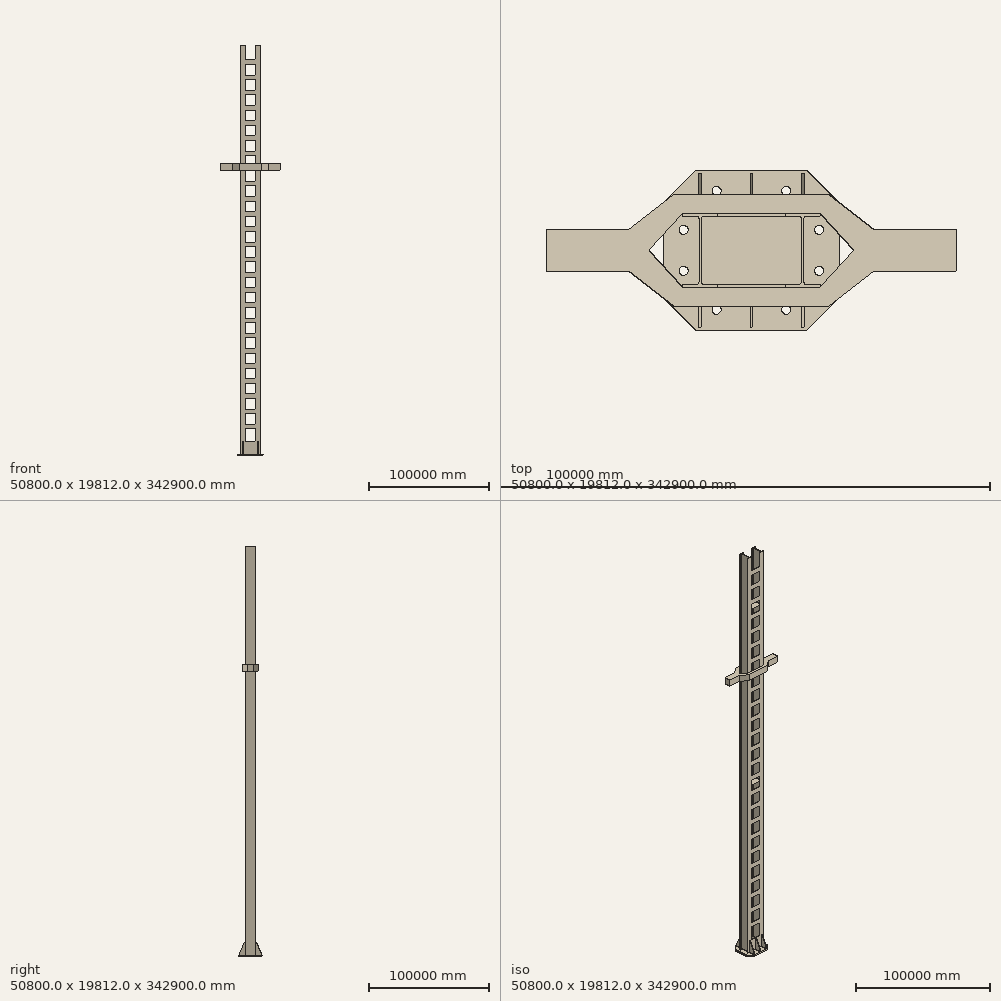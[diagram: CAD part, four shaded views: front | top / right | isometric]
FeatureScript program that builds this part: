
annotation { "Feature Type Name" : "Feature", "Feature Type Description" : "" }
export const myFeature = defineFeature(function(context is Context, id is Id, definition is map)
    precondition{}
    {
        {
            var Q0;
            Q0=qCreatedBy(makeId("Top.planeOp"),FACE);
            var sketch = newSketch(context, id + "F0", { "sketchPlane" : qUnion([Q0])});
            skLineSegment(sketch, "E0", {"start": v(-8509, 4572) * mm, "end": v(8509, 4572) * mm});
            skLineSegment(sketch, "E1", {"start": v(8509, 4572) * mm, "end": v(8509, 4249.42) * mm});
            skLineSegment(sketch, "E2", {"start": v(8509, 4249.42) * mm, "end": v(6908.8, 4249.42) * mm});
            skLineSegment(sketch, "E3", {"start": v(6451.6, 3792.22) * mm, "end": v(6451.6, -3792.22) * mm});
            skLineSegment(sketch, "E4", {"start": v(6908.8, -4249.42) * mm, "end": v(8509, -4249.42) * mm});
            skLineSegment(sketch, "E5", {"start": v(8509, -4249.42) * mm, "end": v(8509, -4572) * mm});
            skLineSegment(sketch, "E6", {"start": v(8509, -4572) * mm, "end": v(-8509, -4572) * mm});
            skLineSegment(sketch, "E7", {"start": v(-8509, -4572) * mm, "end": v(-8509, -4249.42) * mm});
            skLineSegment(sketch, "E8", {"start": v(-8509, -4249.42) * mm, "end": v(-6908.8, -4249.42) * mm});
            skLineSegment(sketch, "E9", {"start": v(-6451.6, -3792.22) * mm, "end": v(-6451.6, 3792.22) * mm});
            skLineSegment(sketch, "E10", {"start": v(-6908.8, 4249.42) * mm, "end": v(-8509, 4249.42) * mm});
            skLineSegment(sketch, "E11", {"start": v(-8509, 4249.42) * mm, "end": v(-8509, 4572) * mm});
            skPoint(sketch, "E12.visualSharp", {"position": v(-6451.6, 4249.42) * mm});
            skArc(sketch, "E12.filletArc", {"start": v(-6451.6, 3792.22) * mm, "mid": v(-6585.51, 4115.5) * mm, "end": v(-6908.8, 4249.42) * mm});
            skPoint(sketch, "E13.visualSharp", {"position": v(6451.6, 4249.42) * mm});
            skArc(sketch, "E13.filletArc", {"start": v(6908.8, 4249.42) * mm, "mid": v(6585.51, 4115.5) * mm, "end": v(6451.6, 3792.22) * mm});
            skPoint(sketch, "E14.visualSharp", {"position": v(6451.6, -4249.42) * mm});
            skArc(sketch, "E14.filletArc", {"start": v(6451.6, -3792.22) * mm, "mid": v(6585.51, -4115.5) * mm, "end": v(6908.8, -4249.42) * mm});
            skPoint(sketch, "E15.visualSharp", {"position": v(-6451.6, -4249.42) * mm});
            skArc(sketch, "E15.filletArc", {"start": v(-6908.8, -4249.42) * mm, "mid": v(-6585.51, -4115.5) * mm, "end": v(-6451.6, -3792.22) * mm});
            skSolve(sketch);
        }
        {
            var Q0;
            Q0=qSketchRegion(id+"F0",true);
            extrude(context, id + "F1", {"entities" : qUnion([Q0]), "depth" : 342900 * mm});
        }
        {
            var Q0;
            Q0=makeQuery(id+"F1.opExtrude","CAP_FACE",FACE,{"disambiguationData":[OSD([sQuery(id+"F0.wireOp",EDGE,"E0"),sQuery(id+"F0.wireOp",EDGE,"E1"),sQuery(id+"F0.wireOp",EDGE,"E2"),sQuery(id+"F0.wireOp",EDGE,"E3"),sQuery(id+"F0.wireOp",EDGE,"E4"),sQuery(id+"F0.wireOp",EDGE,"E5"),sQuery(id+"F0.wireOp",EDGE,"E6"),sQuery(id+"F0.wireOp",EDGE,"E7"),sQuery(id+"F0.wireOp",EDGE,"E8"),sQuery(id+"F0.wireOp",EDGE,"E9"),sQuery(id+"F0.wireOp",EDGE,"E10"),sQuery(id+"F0.wireOp",EDGE,"E11"),sQuery(id+"F0.wireOp",EDGE,"E12.filletArc"),sQuery(id+"F0.wireOp",EDGE,"E13.filletArc"),sQuery(id+"F0.wireOp",EDGE,"E14.filletArc"),sQuery(id+"F0.wireOp",EDGE,"E15.filletArc")])],"isStart":true});
            var sketch = newSketch(context, id + "F2", { "sketchPlane" : qUnion([Q0])});
            skLineSegment(sketch, "E16.bottom", {"start": v(-5791.2, 4249.42) * mm, "end": v(5791.2, 4249.42) * mm});
            skLineSegment(sketch, "E16.top", {"start": v(-5791.2, -4249.42) * mm, "end": v(5791.2, -4249.42) * mm});
            skLineSegment(sketch, "E16.left", {"start": v(-6248.4, 3792.22) * mm, "end": v(-6248.4, -3792.22) * mm});
            skLineSegment(sketch, "E16.right", {"start": v(6248.4, 3792.22) * mm, "end": v(6248.4, -3792.22) * mm});
            skPoint(sketch, "E17.visualSharp", {"position": v(-6248.4, 4249.42) * mm});
            skArc(sketch, "E17.filletArc", {"start": v(-5791.2, 4249.42) * mm, "mid": v(-6114.49, 4115.5) * mm, "end": v(-6248.4, 3792.22) * mm});
            skPoint(sketch, "E18.visualSharp", {"position": v(6248.4, 4249.42) * mm});
            skArc(sketch, "E18.filletArc", {"start": v(6248.4, 3792.22) * mm, "mid": v(6114.49, 4115.5) * mm, "end": v(5791.2, 4249.42) * mm});
            skPoint(sketch, "E19.visualSharp", {"position": v(6248.4, -4249.42) * mm});
            skArc(sketch, "E19.filletArc", {"start": v(5791.2, -4249.42) * mm, "mid": v(6114.49, -4115.5) * mm, "end": v(6248.4, -3792.22) * mm});
            skPoint(sketch, "E20.visualSharp", {"position": v(-6248.4, -4249.42) * mm});
            skArc(sketch, "E20.filletArc", {"start": v(-6248.4, -3792.22) * mm, "mid": v(-6114.49, -4115.5) * mm, "end": v(-5791.2, -4249.42) * mm});
            skLineSegment(sketch, "E21", {"start": v(-6913.3, 0) * mm, "end": v(6813.76, 0) * mm, "construction": true});
            skLineSegment(sketch, "E22", {"start": v(0, 5029.13) * mm, "end": v(0, -5231.93) * mm, "construction": true});
            skSolve(sketch);
        }
        {
            var Q0;
            Q0=qSketchRegion(id+"F2",true);
            extrude(context, id + "F3", {"entities" : qUnion([Q0]), "operationType" : NewBodyOperationType.REMOVE, "endBound" : BoundingType.THROUGH_ALL, "oppositeDirection" : true, "depth" : 25.4 * mm});
        }
        {
            var Q0;
            Q0=makeQuery(id+"F1.opExtrude","SWEPT_FACE",FACE,{"disambiguationData":[OSD([sQuery(id+"F0.wireOp",EDGE,"E6")])]});
            var sketch = newSketch(context, id + "F4", { "sketchPlane" : qUnion([Q0])});
            skLineSegment(sketch, "E23.bottom", {"start": v(-4191, 34925) * mm, "end": v(4191, 34925) * mm});
            skLineSegment(sketch, "E23.top", {"start": v(-4191, 26035) * mm, "end": v(4191, 26035) * mm});
            skLineSegment(sketch, "E23.left", {"start": v(-4191, 34925) * mm, "end": v(-4191, 26035) * mm});
            skLineSegment(sketch, "E23.right", {"start": v(4191, 34925) * mm, "end": v(4191, 26035) * mm});
            skLineSegment(sketch, "E24", {"start": v(0, -2627.58) * mm, "end": v(0, 406140.36) * mm, "construction": true});
            skLineSegment(sketch, "E25.0.1.0", {"start": v(-4191, 47625) * mm, "end": v(4191, 47625) * mm});
            skLineSegment(sketch, "E25.0.1.1", {"start": v(-4191, 38735) * mm, "end": v(4191, 38735) * mm});
            skLineSegment(sketch, "E25.0.1.2", {"start": v(-4191, 47625) * mm, "end": v(-4191, 38735) * mm});
            skLineSegment(sketch, "E25.0.1.3", {"start": v(4191, 47625) * mm, "end": v(4191, 38735) * mm});
            skLineSegment(sketch, "E25.0.2.0", {"start": v(-4191, 60325) * mm, "end": v(4191, 60325) * mm});
            skLineSegment(sketch, "E25.0.2.1", {"start": v(-4191, 51435) * mm, "end": v(4191, 51435) * mm});
            skLineSegment(sketch, "E25.0.2.2", {"start": v(-4191, 60325) * mm, "end": v(-4191, 51435) * mm});
            skLineSegment(sketch, "E25.0.2.3", {"start": v(4191, 60325) * mm, "end": v(4191, 51435) * mm});
            skLineSegment(sketch, "E25.0.3.0", {"start": v(-4191, 73025) * mm, "end": v(4191, 73025) * mm});
            skLineSegment(sketch, "E25.0.3.1", {"start": v(-4191, 64135) * mm, "end": v(4191, 64135) * mm});
            skLineSegment(sketch, "E25.0.3.2", {"start": v(-4191, 73025) * mm, "end": v(-4191, 64135) * mm});
            skLineSegment(sketch, "E25.0.3.3", {"start": v(4191, 73025) * mm, "end": v(4191, 64135) * mm});
            skLineSegment(sketch, "E25.0.4.0", {"start": v(-4191, 85725) * mm, "end": v(4191, 85725) * mm});
            skLineSegment(sketch, "E25.0.4.1", {"start": v(-4191, 76835) * mm, "end": v(4191, 76835) * mm});
            skLineSegment(sketch, "E25.0.4.2", {"start": v(-4191, 85725) * mm, "end": v(-4191, 76835) * mm});
            skLineSegment(sketch, "E25.0.4.3", {"start": v(4191, 85725) * mm, "end": v(4191, 76835) * mm});
            skLineSegment(sketch, "E25.0.5.0", {"start": v(-4191, 98425) * mm, "end": v(4191, 98425) * mm});
            skLineSegment(sketch, "E25.0.5.1", {"start": v(-4191, 89535) * mm, "end": v(4191, 89535) * mm});
            skLineSegment(sketch, "E25.0.5.2", {"start": v(-4191, 98425) * mm, "end": v(-4191, 89535) * mm});
            skLineSegment(sketch, "E25.0.5.3", {"start": v(4191, 98425) * mm, "end": v(4191, 89535) * mm});
            skLineSegment(sketch, "E25.0.6.0", {"start": v(-4191, 111125) * mm, "end": v(4191, 111125) * mm});
            skLineSegment(sketch, "E25.0.6.1", {"start": v(-4191, 102235) * mm, "end": v(4191, 102235) * mm});
            skLineSegment(sketch, "E25.0.6.2", {"start": v(-4191, 111125) * mm, "end": v(-4191, 102235) * mm});
            skLineSegment(sketch, "E25.0.6.3", {"start": v(4191, 111125) * mm, "end": v(4191, 102235) * mm});
            skLineSegment(sketch, "E25.0.7.0", {"start": v(-4191, 123825) * mm, "end": v(4191, 123825) * mm});
            skLineSegment(sketch, "E25.0.7.1", {"start": v(-4191, 114935) * mm, "end": v(4191, 114935) * mm});
            skLineSegment(sketch, "E25.0.7.2", {"start": v(-4191, 123825) * mm, "end": v(-4191, 114935) * mm});
            skLineSegment(sketch, "E25.0.7.3", {"start": v(4191, 123825) * mm, "end": v(4191, 114935) * mm});
            skLineSegment(sketch, "E25.0.8.0", {"start": v(-4191, 136525) * mm, "end": v(4191, 136525) * mm});
            skLineSegment(sketch, "E25.0.8.1", {"start": v(-4191, 127635) * mm, "end": v(4191, 127635) * mm});
            skLineSegment(sketch, "E25.0.8.2", {"start": v(-4191, 136525) * mm, "end": v(-4191, 127635) * mm});
            skLineSegment(sketch, "E25.0.8.3", {"start": v(4191, 136525) * mm, "end": v(4191, 127635) * mm});
            skLineSegment(sketch, "E25.0.9.0", {"start": v(-4191, 149225) * mm, "end": v(4191, 149225) * mm});
            skLineSegment(sketch, "E25.0.9.1", {"start": v(-4191, 140335) * mm, "end": v(4191, 140335) * mm});
            skLineSegment(sketch, "E25.0.9.2", {"start": v(-4191, 149225) * mm, "end": v(-4191, 140335) * mm});
            skLineSegment(sketch, "E25.0.9.3", {"start": v(4191, 149225) * mm, "end": v(4191, 140335) * mm});
            skLineSegment(sketch, "E25.0.10.0", {"start": v(-4191, 161925) * mm, "end": v(4191, 161925) * mm});
            skLineSegment(sketch, "E25.0.10.1", {"start": v(-4191, 153035) * mm, "end": v(4191, 153035) * mm});
            skLineSegment(sketch, "E25.0.10.2", {"start": v(-4191, 161925) * mm, "end": v(-4191, 153035) * mm});
            skLineSegment(sketch, "E25.0.10.3", {"start": v(4191, 161925) * mm, "end": v(4191, 153035) * mm});
            skLineSegment(sketch, "E25.0.11.0", {"start": v(-4191, 174625) * mm, "end": v(4191, 174625) * mm});
            skLineSegment(sketch, "E25.0.11.1", {"start": v(-4191, 165735) * mm, "end": v(4191, 165735) * mm});
            skLineSegment(sketch, "E25.0.11.2", {"start": v(-4191, 174625) * mm, "end": v(-4191, 165735) * mm});
            skLineSegment(sketch, "E25.0.11.3", {"start": v(4191, 174625) * mm, "end": v(4191, 165735) * mm});
            skLineSegment(sketch, "E25.0.12.0", {"start": v(-4191, 187325) * mm, "end": v(4191, 187325) * mm});
            skLineSegment(sketch, "E25.0.12.1", {"start": v(-4191, 178435) * mm, "end": v(4191, 178435) * mm});
            skLineSegment(sketch, "E25.0.12.2", {"start": v(-4191, 187325) * mm, "end": v(-4191, 178435) * mm});
            skLineSegment(sketch, "E25.0.12.3", {"start": v(4191, 187325) * mm, "end": v(4191, 178435) * mm});
            skLineSegment(sketch, "E25.0.13.0", {"start": v(-4191, 200025) * mm, "end": v(4191, 200025) * mm});
            skLineSegment(sketch, "E25.0.13.1", {"start": v(-4191, 191135) * mm, "end": v(4191, 191135) * mm});
            skLineSegment(sketch, "E25.0.13.2", {"start": v(-4191, 200025) * mm, "end": v(-4191, 191135) * mm});
            skLineSegment(sketch, "E25.0.13.3", {"start": v(4191, 200025) * mm, "end": v(4191, 191135) * mm});
            skLineSegment(sketch, "E25.0.14.0", {"start": v(-4191, 212725) * mm, "end": v(4191, 212725) * mm});
            skLineSegment(sketch, "E25.0.14.1", {"start": v(-4191, 203835) * mm, "end": v(4191, 203835) * mm});
            skLineSegment(sketch, "E25.0.14.2", {"start": v(-4191, 212725) * mm, "end": v(-4191, 203835) * mm});
            skLineSegment(sketch, "E25.0.14.3", {"start": v(4191, 212725) * mm, "end": v(4191, 203835) * mm});
            skLineSegment(sketch, "E25.0.15.0", {"start": v(-4191, 225425) * mm, "end": v(4191, 225425) * mm});
            skLineSegment(sketch, "E25.0.15.1", {"start": v(-4191, 216535) * mm, "end": v(4191, 216535) * mm});
            skLineSegment(sketch, "E25.0.15.2", {"start": v(-4191, 225425) * mm, "end": v(-4191, 216535) * mm});
            skLineSegment(sketch, "E25.0.15.3", {"start": v(4191, 225425) * mm, "end": v(4191, 216535) * mm});
            skLineSegment(sketch, "E25.0.16.0", {"start": v(-4191, 238125) * mm, "end": v(4191, 238125) * mm});
            skLineSegment(sketch, "E25.0.16.1", {"start": v(-4191, 229235) * mm, "end": v(4191, 229235) * mm});
            skLineSegment(sketch, "E25.0.16.2", {"start": v(-4191, 238125) * mm, "end": v(-4191, 229235) * mm});
            skLineSegment(sketch, "E25.0.16.3", {"start": v(4191, 238125) * mm, "end": v(4191, 229235) * mm});
            skLineSegment(sketch, "E25.0.17.0", {"start": v(-4191, 250825) * mm, "end": v(4191, 250825) * mm});
            skLineSegment(sketch, "E25.0.17.1", {"start": v(-4191, 241935) * mm, "end": v(4191, 241935) * mm});
            skLineSegment(sketch, "E25.0.17.2", {"start": v(-4191, 250825) * mm, "end": v(-4191, 241935) * mm});
            skLineSegment(sketch, "E25.0.17.3", {"start": v(4191, 250825) * mm, "end": v(4191, 241935) * mm});
            skLineSegment(sketch, "E25.0.18.0", {"start": v(-4191, 263525) * mm, "end": v(4191, 263525) * mm});
            skLineSegment(sketch, "E25.0.18.1", {"start": v(-4191, 254635) * mm, "end": v(4191, 254635) * mm});
            skLineSegment(sketch, "E25.0.18.2", {"start": v(-4191, 263525) * mm, "end": v(-4191, 254635) * mm});
            skLineSegment(sketch, "E25.0.18.3", {"start": v(4191, 263525) * mm, "end": v(4191, 254635) * mm});
            skLineSegment(sketch, "E25.0.19.0", {"start": v(-4191, 276225) * mm, "end": v(4191, 276225) * mm});
            skLineSegment(sketch, "E25.0.19.1", {"start": v(-4191, 267335) * mm, "end": v(4191, 267335) * mm});
            skLineSegment(sketch, "E25.0.19.2", {"start": v(-4191, 276225) * mm, "end": v(-4191, 267335) * mm});
            skLineSegment(sketch, "E25.0.19.3", {"start": v(4191, 276225) * mm, "end": v(4191, 267335) * mm});
            skLineSegment(sketch, "E25.0.20.0", {"start": v(-4191, 288925) * mm, "end": v(4191, 288925) * mm});
            skLineSegment(sketch, "E25.0.20.1", {"start": v(-4191, 280035) * mm, "end": v(4191, 280035) * mm});
            skLineSegment(sketch, "E25.0.20.2", {"start": v(-4191, 288925) * mm, "end": v(-4191, 280035) * mm});
            skLineSegment(sketch, "E25.0.20.3", {"start": v(4191, 288925) * mm, "end": v(4191, 280035) * mm});
            skLineSegment(sketch, "E25.0.21.0", {"start": v(-4191, 301625) * mm, "end": v(4191, 301625) * mm});
            skLineSegment(sketch, "E25.0.21.1", {"start": v(-4191, 292735) * mm, "end": v(4191, 292735) * mm});
            skLineSegment(sketch, "E25.0.21.2", {"start": v(-4191, 301625) * mm, "end": v(-4191, 292735) * mm});
            skLineSegment(sketch, "E25.0.21.3", {"start": v(4191, 301625) * mm, "end": v(4191, 292735) * mm});
            skLineSegment(sketch, "E25.0.22.0", {"start": v(-4191, 314325) * mm, "end": v(4191, 314325) * mm});
            skLineSegment(sketch, "E25.0.22.1", {"start": v(-4191, 305435) * mm, "end": v(4191, 305435) * mm});
            skLineSegment(sketch, "E25.0.22.2", {"start": v(-4191, 314325) * mm, "end": v(-4191, 305435) * mm});
            skLineSegment(sketch, "E25.0.22.3", {"start": v(4191, 314325) * mm, "end": v(4191, 305435) * mm});
            skLineSegment(sketch, "E25.0.23.0", {"start": v(-4191, 327025) * mm, "end": v(4191, 327025) * mm});
            skLineSegment(sketch, "E25.0.23.1", {"start": v(-4191, 318135) * mm, "end": v(4191, 318135) * mm});
            skLineSegment(sketch, "E25.0.23.2", {"start": v(-4191, 327025) * mm, "end": v(-4191, 318135) * mm});
            skLineSegment(sketch, "E25.0.23.3", {"start": v(4191, 327025) * mm, "end": v(4191, 318135) * mm});
            skLineSegment(sketch, "E25.1.1.0", {"start": v(-4191, 47625) * mm, "end": v(4191, 47625) * mm});
            skLineSegment(sketch, "E25.1.1.1", {"start": v(-4191, 38735) * mm, "end": v(4191, 38735) * mm});
            skLineSegment(sketch, "E25.1.1.2", {"start": v(-4191, 47625) * mm, "end": v(-4191, 38735) * mm});
            skLineSegment(sketch, "E25.1.1.3", {"start": v(4191, 47625) * mm, "end": v(4191, 38735) * mm});
            skLineSegment(sketch, "E25.1.2.0", {"start": v(-4191, 60325) * mm, "end": v(4191, 60325) * mm});
            skLineSegment(sketch, "E25.1.2.1", {"start": v(-4191, 51435) * mm, "end": v(4191, 51435) * mm});
            skLineSegment(sketch, "E25.1.2.2", {"start": v(-4191, 60325) * mm, "end": v(-4191, 51435) * mm});
            skLineSegment(sketch, "E25.1.2.3", {"start": v(4191, 60325) * mm, "end": v(4191, 51435) * mm});
            skLineSegment(sketch, "E25.1.3.0", {"start": v(-4191, 73025) * mm, "end": v(4191, 73025) * mm});
            skLineSegment(sketch, "E25.1.3.1", {"start": v(-4191, 64135) * mm, "end": v(4191, 64135) * mm});
            skLineSegment(sketch, "E25.1.3.2", {"start": v(-4191, 73025) * mm, "end": v(-4191, 64135) * mm});
            skLineSegment(sketch, "E25.1.3.3", {"start": v(4191, 73025) * mm, "end": v(4191, 64135) * mm});
            skLineSegment(sketch, "E25.1.4.0", {"start": v(-4191, 85725) * mm, "end": v(4191, 85725) * mm});
            skLineSegment(sketch, "E25.1.4.1", {"start": v(-4191, 76835) * mm, "end": v(4191, 76835) * mm});
            skLineSegment(sketch, "E25.1.4.2", {"start": v(-4191, 85725) * mm, "end": v(-4191, 76835) * mm});
            skLineSegment(sketch, "E25.1.4.3", {"start": v(4191, 85725) * mm, "end": v(4191, 76835) * mm});
            skLineSegment(sketch, "E25.1.5.0", {"start": v(-4191, 98425) * mm, "end": v(4191, 98425) * mm});
            skLineSegment(sketch, "E25.1.5.1", {"start": v(-4191, 89535) * mm, "end": v(4191, 89535) * mm});
            skLineSegment(sketch, "E25.1.5.2", {"start": v(-4191, 98425) * mm, "end": v(-4191, 89535) * mm});
            skLineSegment(sketch, "E25.1.5.3", {"start": v(4191, 98425) * mm, "end": v(4191, 89535) * mm});
            skLineSegment(sketch, "E25.1.6.0", {"start": v(-4191, 111125) * mm, "end": v(4191, 111125) * mm});
            skLineSegment(sketch, "E25.1.6.1", {"start": v(-4191, 102235) * mm, "end": v(4191, 102235) * mm});
            skLineSegment(sketch, "E25.1.6.2", {"start": v(-4191, 111125) * mm, "end": v(-4191, 102235) * mm});
            skLineSegment(sketch, "E25.1.6.3", {"start": v(4191, 111125) * mm, "end": v(4191, 102235) * mm});
            skLineSegment(sketch, "E25.1.7.0", {"start": v(-4191, 123825) * mm, "end": v(4191, 123825) * mm});
            skLineSegment(sketch, "E25.1.7.1", {"start": v(-4191, 114935) * mm, "end": v(4191, 114935) * mm});
            skLineSegment(sketch, "E25.1.7.2", {"start": v(-4191, 123825) * mm, "end": v(-4191, 114935) * mm});
            skLineSegment(sketch, "E25.1.7.3", {"start": v(4191, 123825) * mm, "end": v(4191, 114935) * mm});
            skLineSegment(sketch, "E25.1.8.0", {"start": v(-4191, 136525) * mm, "end": v(4191, 136525) * mm});
            skLineSegment(sketch, "E25.1.8.1", {"start": v(-4191, 127635) * mm, "end": v(4191, 127635) * mm});
            skLineSegment(sketch, "E25.1.8.2", {"start": v(-4191, 136525) * mm, "end": v(-4191, 127635) * mm});
            skLineSegment(sketch, "E25.1.8.3", {"start": v(4191, 136525) * mm, "end": v(4191, 127635) * mm});
            skLineSegment(sketch, "E25.1.9.0", {"start": v(-4191, 149225) * mm, "end": v(4191, 149225) * mm});
            skLineSegment(sketch, "E25.1.9.1", {"start": v(-4191, 140335) * mm, "end": v(4191, 140335) * mm});
            skLineSegment(sketch, "E25.1.9.2", {"start": v(-4191, 149225) * mm, "end": v(-4191, 140335) * mm});
            skLineSegment(sketch, "E25.1.9.3", {"start": v(4191, 149225) * mm, "end": v(4191, 140335) * mm});
            skLineSegment(sketch, "E25.1.10.0", {"start": v(-4191, 161925) * mm, "end": v(4191, 161925) * mm});
            skLineSegment(sketch, "E25.1.10.1", {"start": v(-4191, 153035) * mm, "end": v(4191, 153035) * mm});
            skLineSegment(sketch, "E25.1.10.2", {"start": v(-4191, 161925) * mm, "end": v(-4191, 153035) * mm});
            skLineSegment(sketch, "E25.1.10.3", {"start": v(4191, 161925) * mm, "end": v(4191, 153035) * mm});
            skLineSegment(sketch, "E25.1.11.0", {"start": v(-4191, 174625) * mm, "end": v(4191, 174625) * mm});
            skLineSegment(sketch, "E25.1.11.1", {"start": v(-4191, 165735) * mm, "end": v(4191, 165735) * mm});
            skLineSegment(sketch, "E25.1.11.2", {"start": v(-4191, 174625) * mm, "end": v(-4191, 165735) * mm});
            skLineSegment(sketch, "E25.1.11.3", {"start": v(4191, 174625) * mm, "end": v(4191, 165735) * mm});
            skLineSegment(sketch, "E25.1.12.0", {"start": v(-4191, 187325) * mm, "end": v(4191, 187325) * mm});
            skLineSegment(sketch, "E25.1.12.1", {"start": v(-4191, 178435) * mm, "end": v(4191, 178435) * mm});
            skLineSegment(sketch, "E25.1.12.2", {"start": v(-4191, 187325) * mm, "end": v(-4191, 178435) * mm});
            skLineSegment(sketch, "E25.1.12.3", {"start": v(4191, 187325) * mm, "end": v(4191, 178435) * mm});
            skLineSegment(sketch, "E25.1.13.0", {"start": v(-4191, 200025) * mm, "end": v(4191, 200025) * mm});
            skLineSegment(sketch, "E25.1.13.1", {"start": v(-4191, 191135) * mm, "end": v(4191, 191135) * mm});
            skLineSegment(sketch, "E25.1.13.2", {"start": v(-4191, 200025) * mm, "end": v(-4191, 191135) * mm});
            skLineSegment(sketch, "E25.1.13.3", {"start": v(4191, 200025) * mm, "end": v(4191, 191135) * mm});
            skLineSegment(sketch, "E25.1.14.0", {"start": v(-4191, 212725) * mm, "end": v(4191, 212725) * mm});
            skLineSegment(sketch, "E25.1.14.1", {"start": v(-4191, 203835) * mm, "end": v(4191, 203835) * mm});
            skLineSegment(sketch, "E25.1.14.2", {"start": v(-4191, 212725) * mm, "end": v(-4191, 203835) * mm});
            skLineSegment(sketch, "E25.1.14.3", {"start": v(4191, 212725) * mm, "end": v(4191, 203835) * mm});
            skLineSegment(sketch, "E25.1.15.0", {"start": v(-4191, 225425) * mm, "end": v(4191, 225425) * mm});
            skLineSegment(sketch, "E25.1.15.1", {"start": v(-4191, 216535) * mm, "end": v(4191, 216535) * mm});
            skLineSegment(sketch, "E25.1.15.2", {"start": v(-4191, 225425) * mm, "end": v(-4191, 216535) * mm});
            skLineSegment(sketch, "E25.1.15.3", {"start": v(4191, 225425) * mm, "end": v(4191, 216535) * mm});
            skLineSegment(sketch, "E25.1.16.0", {"start": v(-4191, 238125) * mm, "end": v(4191, 238125) * mm});
            skLineSegment(sketch, "E25.1.16.1", {"start": v(-4191, 229235) * mm, "end": v(4191, 229235) * mm});
            skLineSegment(sketch, "E25.1.16.2", {"start": v(-4191, 238125) * mm, "end": v(-4191, 229235) * mm});
            skLineSegment(sketch, "E25.1.16.3", {"start": v(4191, 238125) * mm, "end": v(4191, 229235) * mm});
            skLineSegment(sketch, "E25.1.17.0", {"start": v(-4191, 250825) * mm, "end": v(4191, 250825) * mm});
            skLineSegment(sketch, "E25.1.17.1", {"start": v(-4191, 241935) * mm, "end": v(4191, 241935) * mm});
            skLineSegment(sketch, "E25.1.17.2", {"start": v(-4191, 250825) * mm, "end": v(-4191, 241935) * mm});
            skLineSegment(sketch, "E25.1.17.3", {"start": v(4191, 250825) * mm, "end": v(4191, 241935) * mm});
            skLineSegment(sketch, "E25.1.18.0", {"start": v(-4191, 263525) * mm, "end": v(4191, 263525) * mm});
            skLineSegment(sketch, "E25.1.18.1", {"start": v(-4191, 254635) * mm, "end": v(4191, 254635) * mm});
            skLineSegment(sketch, "E25.1.18.2", {"start": v(-4191, 263525) * mm, "end": v(-4191, 254635) * mm});
            skLineSegment(sketch, "E25.1.18.3", {"start": v(4191, 263525) * mm, "end": v(4191, 254635) * mm});
            skLineSegment(sketch, "E25.1.19.0", {"start": v(-4191, 276225) * mm, "end": v(4191, 276225) * mm});
            skLineSegment(sketch, "E25.1.19.1", {"start": v(-4191, 267335) * mm, "end": v(4191, 267335) * mm});
            skLineSegment(sketch, "E25.1.19.2", {"start": v(-4191, 276225) * mm, "end": v(-4191, 267335) * mm});
            skLineSegment(sketch, "E25.1.19.3", {"start": v(4191, 276225) * mm, "end": v(4191, 267335) * mm});
            skLineSegment(sketch, "E25.1.20.0", {"start": v(-4191, 288925) * mm, "end": v(4191, 288925) * mm});
            skLineSegment(sketch, "E25.1.20.1", {"start": v(-4191, 280035) * mm, "end": v(4191, 280035) * mm});
            skLineSegment(sketch, "E25.1.20.2", {"start": v(-4191, 288925) * mm, "end": v(-4191, 280035) * mm});
            skLineSegment(sketch, "E25.1.20.3", {"start": v(4191, 288925) * mm, "end": v(4191, 280035) * mm});
            skLineSegment(sketch, "E25.1.21.0", {"start": v(-4191, 301625) * mm, "end": v(4191, 301625) * mm});
            skLineSegment(sketch, "E25.1.21.1", {"start": v(-4191, 292735) * mm, "end": v(4191, 292735) * mm});
            skLineSegment(sketch, "E25.1.21.2", {"start": v(-4191, 301625) * mm, "end": v(-4191, 292735) * mm});
            skLineSegment(sketch, "E25.1.21.3", {"start": v(4191, 301625) * mm, "end": v(4191, 292735) * mm});
            skLineSegment(sketch, "E25.1.22.0", {"start": v(-4191, 314325) * mm, "end": v(4191, 314325) * mm});
            skLineSegment(sketch, "E25.1.22.1", {"start": v(-4191, 305435) * mm, "end": v(4191, 305435) * mm});
            skLineSegment(sketch, "E25.1.22.2", {"start": v(-4191, 314325) * mm, "end": v(-4191, 305435) * mm});
            skLineSegment(sketch, "E25.1.22.3", {"start": v(4191, 314325) * mm, "end": v(4191, 305435) * mm});
            skLineSegment(sketch, "E25.1.23.0", {"start": v(-4191, 327025) * mm, "end": v(4191, 327025) * mm});
            skLineSegment(sketch, "E25.1.23.1", {"start": v(-4191, 318135) * mm, "end": v(4191, 318135) * mm});
            skLineSegment(sketch, "E25.1.23.2", {"start": v(-4191, 327025) * mm, "end": v(-4191, 318135) * mm});
            skLineSegment(sketch, "E25.1.23.3", {"start": v(4191, 327025) * mm, "end": v(4191, 318135) * mm});
            skLineSegment(sketch, "E25.2.1.0", {"start": v(-4191, 47625) * mm, "end": v(4191, 47625) * mm});
            skLineSegment(sketch, "E25.2.1.1", {"start": v(-4191, 38735) * mm, "end": v(4191, 38735) * mm});
            skLineSegment(sketch, "E25.2.1.2", {"start": v(-4191, 47625) * mm, "end": v(-4191, 38735) * mm});
            skLineSegment(sketch, "E25.2.1.3", {"start": v(4191, 47625) * mm, "end": v(4191, 38735) * mm});
            skLineSegment(sketch, "E25.2.2.0", {"start": v(-4191, 60325) * mm, "end": v(4191, 60325) * mm});
            skLineSegment(sketch, "E25.2.2.1", {"start": v(-4191, 51435) * mm, "end": v(4191, 51435) * mm});
            skLineSegment(sketch, "E25.2.2.2", {"start": v(-4191, 60325) * mm, "end": v(-4191, 51435) * mm});
            skLineSegment(sketch, "E25.2.2.3", {"start": v(4191, 60325) * mm, "end": v(4191, 51435) * mm});
            skLineSegment(sketch, "E25.2.3.0", {"start": v(-4191, 73025) * mm, "end": v(4191, 73025) * mm});
            skLineSegment(sketch, "E25.2.3.1", {"start": v(-4191, 64135) * mm, "end": v(4191, 64135) * mm});
            skLineSegment(sketch, "E25.2.3.2", {"start": v(-4191, 73025) * mm, "end": v(-4191, 64135) * mm});
            skLineSegment(sketch, "E25.2.3.3", {"start": v(4191, 73025) * mm, "end": v(4191, 64135) * mm});
            skLineSegment(sketch, "E25.2.4.0", {"start": v(-4191, 85725) * mm, "end": v(4191, 85725) * mm});
            skLineSegment(sketch, "E25.2.4.1", {"start": v(-4191, 76835) * mm, "end": v(4191, 76835) * mm});
            skLineSegment(sketch, "E25.2.4.2", {"start": v(-4191, 85725) * mm, "end": v(-4191, 76835) * mm});
            skLineSegment(sketch, "E25.2.4.3", {"start": v(4191, 85725) * mm, "end": v(4191, 76835) * mm});
            skLineSegment(sketch, "E25.2.5.0", {"start": v(-4191, 98425) * mm, "end": v(4191, 98425) * mm});
            skLineSegment(sketch, "E25.2.5.1", {"start": v(-4191, 89535) * mm, "end": v(4191, 89535) * mm});
            skLineSegment(sketch, "E25.2.5.2", {"start": v(-4191, 98425) * mm, "end": v(-4191, 89535) * mm});
            skLineSegment(sketch, "E25.2.5.3", {"start": v(4191, 98425) * mm, "end": v(4191, 89535) * mm});
            skLineSegment(sketch, "E25.2.6.0", {"start": v(-4191, 111125) * mm, "end": v(4191, 111125) * mm});
            skLineSegment(sketch, "E25.2.6.1", {"start": v(-4191, 102235) * mm, "end": v(4191, 102235) * mm});
            skLineSegment(sketch, "E25.2.6.2", {"start": v(-4191, 111125) * mm, "end": v(-4191, 102235) * mm});
            skLineSegment(sketch, "E25.2.6.3", {"start": v(4191, 111125) * mm, "end": v(4191, 102235) * mm});
            skLineSegment(sketch, "E25.2.7.0", {"start": v(-4191, 123825) * mm, "end": v(4191, 123825) * mm});
            skLineSegment(sketch, "E25.2.7.1", {"start": v(-4191, 114935) * mm, "end": v(4191, 114935) * mm});
            skLineSegment(sketch, "E25.2.7.2", {"start": v(-4191, 123825) * mm, "end": v(-4191, 114935) * mm});
            skLineSegment(sketch, "E25.2.7.3", {"start": v(4191, 123825) * mm, "end": v(4191, 114935) * mm});
            skLineSegment(sketch, "E25.2.8.0", {"start": v(-4191, 136525) * mm, "end": v(4191, 136525) * mm});
            skLineSegment(sketch, "E25.2.8.1", {"start": v(-4191, 127635) * mm, "end": v(4191, 127635) * mm});
            skLineSegment(sketch, "E25.2.8.2", {"start": v(-4191, 136525) * mm, "end": v(-4191, 127635) * mm});
            skLineSegment(sketch, "E25.2.8.3", {"start": v(4191, 136525) * mm, "end": v(4191, 127635) * mm});
            skLineSegment(sketch, "E25.2.9.0", {"start": v(-4191, 149225) * mm, "end": v(4191, 149225) * mm});
            skLineSegment(sketch, "E25.2.9.1", {"start": v(-4191, 140335) * mm, "end": v(4191, 140335) * mm});
            skLineSegment(sketch, "E25.2.9.2", {"start": v(-4191, 149225) * mm, "end": v(-4191, 140335) * mm});
            skLineSegment(sketch, "E25.2.9.3", {"start": v(4191, 149225) * mm, "end": v(4191, 140335) * mm});
            skLineSegment(sketch, "E25.2.10.0", {"start": v(-4191, 161925) * mm, "end": v(4191, 161925) * mm});
            skLineSegment(sketch, "E25.2.10.1", {"start": v(-4191, 153035) * mm, "end": v(4191, 153035) * mm});
            skLineSegment(sketch, "E25.2.10.2", {"start": v(-4191, 161925) * mm, "end": v(-4191, 153035) * mm});
            skLineSegment(sketch, "E25.2.10.3", {"start": v(4191, 161925) * mm, "end": v(4191, 153035) * mm});
            skLineSegment(sketch, "E25.2.11.0", {"start": v(-4191, 174625) * mm, "end": v(4191, 174625) * mm});
            skLineSegment(sketch, "E25.2.11.1", {"start": v(-4191, 165735) * mm, "end": v(4191, 165735) * mm});
            skLineSegment(sketch, "E25.2.11.2", {"start": v(-4191, 174625) * mm, "end": v(-4191, 165735) * mm});
            skLineSegment(sketch, "E25.2.11.3", {"start": v(4191, 174625) * mm, "end": v(4191, 165735) * mm});
            skLineSegment(sketch, "E25.2.12.0", {"start": v(-4191, 187325) * mm, "end": v(4191, 187325) * mm});
            skLineSegment(sketch, "E25.2.12.1", {"start": v(-4191, 178435) * mm, "end": v(4191, 178435) * mm});
            skLineSegment(sketch, "E25.2.12.2", {"start": v(-4191, 187325) * mm, "end": v(-4191, 178435) * mm});
            skLineSegment(sketch, "E25.2.12.3", {"start": v(4191, 187325) * mm, "end": v(4191, 178435) * mm});
            skLineSegment(sketch, "E25.2.13.0", {"start": v(-4191, 200025) * mm, "end": v(4191, 200025) * mm});
            skLineSegment(sketch, "E25.2.13.1", {"start": v(-4191, 191135) * mm, "end": v(4191, 191135) * mm});
            skLineSegment(sketch, "E25.2.13.2", {"start": v(-4191, 200025) * mm, "end": v(-4191, 191135) * mm});
            skLineSegment(sketch, "E25.2.13.3", {"start": v(4191, 200025) * mm, "end": v(4191, 191135) * mm});
            skLineSegment(sketch, "E25.2.14.0", {"start": v(-4191, 212725) * mm, "end": v(4191, 212725) * mm});
            skLineSegment(sketch, "E25.2.14.1", {"start": v(-4191, 203835) * mm, "end": v(4191, 203835) * mm});
            skLineSegment(sketch, "E25.2.14.2", {"start": v(-4191, 212725) * mm, "end": v(-4191, 203835) * mm});
            skLineSegment(sketch, "E25.2.14.3", {"start": v(4191, 212725) * mm, "end": v(4191, 203835) * mm});
            skLineSegment(sketch, "E25.2.15.0", {"start": v(-4191, 225425) * mm, "end": v(4191, 225425) * mm});
            skLineSegment(sketch, "E25.2.15.1", {"start": v(-4191, 216535) * mm, "end": v(4191, 216535) * mm});
            skLineSegment(sketch, "E25.2.15.2", {"start": v(-4191, 225425) * mm, "end": v(-4191, 216535) * mm});
            skLineSegment(sketch, "E25.2.15.3", {"start": v(4191, 225425) * mm, "end": v(4191, 216535) * mm});
            skLineSegment(sketch, "E25.2.16.0", {"start": v(-4191, 238125) * mm, "end": v(4191, 238125) * mm});
            skLineSegment(sketch, "E25.2.16.1", {"start": v(-4191, 229235) * mm, "end": v(4191, 229235) * mm});
            skLineSegment(sketch, "E25.2.16.2", {"start": v(-4191, 238125) * mm, "end": v(-4191, 229235) * mm});
            skLineSegment(sketch, "E25.2.16.3", {"start": v(4191, 238125) * mm, "end": v(4191, 229235) * mm});
            skLineSegment(sketch, "E25.2.17.0", {"start": v(-4191, 250825) * mm, "end": v(4191, 250825) * mm});
            skLineSegment(sketch, "E25.2.17.1", {"start": v(-4191, 241935) * mm, "end": v(4191, 241935) * mm});
            skLineSegment(sketch, "E25.2.17.2", {"start": v(-4191, 250825) * mm, "end": v(-4191, 241935) * mm});
            skLineSegment(sketch, "E25.2.17.3", {"start": v(4191, 250825) * mm, "end": v(4191, 241935) * mm});
            skLineSegment(sketch, "E25.2.18.0", {"start": v(-4191, 263525) * mm, "end": v(4191, 263525) * mm});
            skLineSegment(sketch, "E25.2.18.1", {"start": v(-4191, 254635) * mm, "end": v(4191, 254635) * mm});
            skLineSegment(sketch, "E25.2.18.2", {"start": v(-4191, 263525) * mm, "end": v(-4191, 254635) * mm});
            skLineSegment(sketch, "E25.2.18.3", {"start": v(4191, 263525) * mm, "end": v(4191, 254635) * mm});
            skLineSegment(sketch, "E25.2.19.0", {"start": v(-4191, 276225) * mm, "end": v(4191, 276225) * mm});
            skLineSegment(sketch, "E25.2.19.1", {"start": v(-4191, 267335) * mm, "end": v(4191, 267335) * mm});
            skLineSegment(sketch, "E25.2.19.2", {"start": v(-4191, 276225) * mm, "end": v(-4191, 267335) * mm});
            skLineSegment(sketch, "E25.2.19.3", {"start": v(4191, 276225) * mm, "end": v(4191, 267335) * mm});
            skLineSegment(sketch, "E25.2.20.0", {"start": v(-4191, 288925) * mm, "end": v(4191, 288925) * mm});
            skLineSegment(sketch, "E25.2.20.1", {"start": v(-4191, 280035) * mm, "end": v(4191, 280035) * mm});
            skLineSegment(sketch, "E25.2.20.2", {"start": v(-4191, 288925) * mm, "end": v(-4191, 280035) * mm});
            skLineSegment(sketch, "E25.2.20.3", {"start": v(4191, 288925) * mm, "end": v(4191, 280035) * mm});
            skLineSegment(sketch, "E25.2.21.0", {"start": v(-4191, 301625) * mm, "end": v(4191, 301625) * mm});
            skLineSegment(sketch, "E25.2.21.1", {"start": v(-4191, 292735) * mm, "end": v(4191, 292735) * mm});
            skLineSegment(sketch, "E25.2.21.2", {"start": v(-4191, 301625) * mm, "end": v(-4191, 292735) * mm});
            skLineSegment(sketch, "E25.2.21.3", {"start": v(4191, 301625) * mm, "end": v(4191, 292735) * mm});
            skLineSegment(sketch, "E25.2.22.0", {"start": v(-4191, 314325) * mm, "end": v(4191, 314325) * mm});
            skLineSegment(sketch, "E25.2.22.1", {"start": v(-4191, 305435) * mm, "end": v(4191, 305435) * mm});
            skLineSegment(sketch, "E25.2.22.2", {"start": v(-4191, 314325) * mm, "end": v(-4191, 305435) * mm});
            skLineSegment(sketch, "E25.2.22.3", {"start": v(4191, 314325) * mm, "end": v(4191, 305435) * mm});
            skLineSegment(sketch, "E25.2.23.0", {"start": v(-4191, 327025) * mm, "end": v(4191, 327025) * mm});
            skLineSegment(sketch, "E25.2.23.1", {"start": v(-4191, 318135) * mm, "end": v(4191, 318135) * mm});
            skLineSegment(sketch, "E25.2.23.2", {"start": v(-4191, 327025) * mm, "end": v(-4191, 318135) * mm});
            skLineSegment(sketch, "E25.2.23.3", {"start": v(4191, 327025) * mm, "end": v(4191, 318135) * mm});
            skLineSegment(sketch, "E25.direction1", {"start": v(-4191, 26035) * mm, "end": v(-4191, 26035) * mm});
            skLineSegment(sketch, "E25.direction2", {"start": v(-4191, 26035) * mm, "end": v(-4191, 38735) * mm, "construction": true});
            skLineSegment(sketch, "E26.bottom", {"start": v(-4191, 342900) * mm, "end": v(4191, 342900) * mm});
            skLineSegment(sketch, "E26.top", {"start": v(-4191, 330835) * mm, "end": v(4191, 330835) * mm});
            skLineSegment(sketch, "E26.left", {"start": v(-4191, 342900) * mm, "end": v(-4191, 330835) * mm});
            skLineSegment(sketch, "E26.right", {"start": v(4191, 342900) * mm, "end": v(4191, 330835) * mm});
            skLineSegment(sketch, "E27.bottom", {"start": v(-4191, 22225) * mm, "end": v(4191, 22225) * mm});
            skLineSegment(sketch, "E27.top", {"start": v(-4191, 11303) * mm, "end": v(4191, 11303) * mm});
            skLineSegment(sketch, "E27.left", {"start": v(-4191, 22225) * mm, "end": v(-4191, 11303) * mm});
            skLineSegment(sketch, "E27.right", {"start": v(4191, 22225) * mm, "end": v(4191, 11303) * mm});
            skSolve(sketch);
        }
        {
            var Q0;
            Q0=qSketchRegion(id+"F4",true);
            extrude(context, id + "F5", {"entities" : qUnion([Q0]), "operationType" : NewBodyOperationType.REMOVE, "endBound" : BoundingType.THROUGH_ALL, "oppositeDirection" : true, "depth" : 25.4 * mm});
        }
        {
            var Q0;
            Q0=qCreatedBy(makeId("Top.planeOp"),FACE);
            cPlane(context, id + "F6", {"entities" : qUnion([Q0]), "cplaneType" : CPlaneType.OFFSET, "offset" : 144780 * mm, "width" : 152.4 * mm, "height" : 152.4 * mm});
        }
        {
            var Q0;
            Q0=qCreatedBy(id+"F6.planeOp",FACE);
            var sketch = newSketch(context, id + "F7", { "sketchPlane" : qUnion([Q0])});
            skLineSegment(sketch, "E28", {"start": v(0, 5038.5) * mm, "end": v(0, -5387.54) * mm, "construction": true});
            skLineSegment(sketch, "E29", {"start": v(-6816.57, 0) * mm, "end": v(7079.48, 0) * mm, "construction": true});
            skLineSegment(sketch, "E30.bottom", {"start": v(-5791.2, 4249.42) * mm, "end": v(5791.2, 4249.42) * mm});
            skLineSegment(sketch, "E30.top", {"start": v(-5791.2, -4249.42) * mm, "end": v(5791.2, -4249.42) * mm});
            skLineSegment(sketch, "E30.left", {"start": v(-6248.4, 3792.22) * mm, "end": v(-6248.4, -3792.22) * mm});
            skLineSegment(sketch, "E30.right", {"start": v(6248.4, 3792.22) * mm, "end": v(6248.4, -3792.22) * mm});
            skPoint(sketch, "E31.visualSharp", {"position": v(-6248.4, 4249.42) * mm});
            skArc(sketch, "E31.filletArc", {"start": v(-5791.2, 4249.42) * mm, "mid": v(-6114.49, 4115.5) * mm, "end": v(-6248.4, 3792.22) * mm});
            skPoint(sketch, "E32.visualSharp", {"position": v(6248.4, 4249.42) * mm});
            skArc(sketch, "E32.filletArc", {"start": v(6248.4, 3792.22) * mm, "mid": v(6114.49, 4115.5) * mm, "end": v(5791.2, 4249.42) * mm});
            skPoint(sketch, "E33.visualSharp", {"position": v(6248.4, -4249.42) * mm});
            skArc(sketch, "E33.filletArc", {"start": v(5791.2, -4249.42) * mm, "mid": v(6114.49, -4115.5) * mm, "end": v(6248.4, -3792.22) * mm});
            skPoint(sketch, "E34.visualSharp", {"position": v(-6248.4, -4249.42) * mm});
            skArc(sketch, "E34.filletArc", {"start": v(-6248.4, -3792.22) * mm, "mid": v(-6114.49, -4115.5) * mm, "end": v(-5791.2, -4249.42) * mm});
            skSolve(sketch);
        }
        {
            var Q0;
            Q0=qSketchRegion(id+"F7",true);
            extrude(context, id + "F8", {"entities" : qUnion([Q0]), "operationType" : NewBodyOperationType.ADD, "endBound" : BoundingType.SYMMETRIC, "depth" : 152.4 * mm});
        }
        {
            var Q0;
            Q0=qCreatedBy(makeId("Top.planeOp"),FACE);
            cPlane(context, id + "F9", {"entities" : qUnion([Q0]), "cplaneType" : CPlaneType.OFFSET, "offset" : 297180 * mm, "width" : 152.4 * mm, "height" : 152.4 * mm});
        }
        {
            var Q0;
            Q0=qCreatedBy(id+"F9.planeOp",FACE);
            var sketch = newSketch(context, id + "F10", { "sketchPlane" : qUnion([Q0])});
            skLineSegment(sketch, "E35.bottom", {"start": v(-5791.2, 4249.42) * mm, "end": v(5791.2, 4249.42) * mm});
            skLineSegment(sketch, "E35.top", {"start": v(-5791.2, -4249.42) * mm, "end": v(5791.2, -4249.42) * mm});
            skLineSegment(sketch, "E35.left", {"start": v(-6248.4, 3792.22) * mm, "end": v(-6248.4, -3792.22) * mm});
            skLineSegment(sketch, "E35.right", {"start": v(6248.4, 3792.22) * mm, "end": v(6248.4, -3792.22) * mm});
            skLineSegment(sketch, "E36", {"start": v(-6862.25, 0) * mm, "end": v(7060.04, 0) * mm, "construction": true});
            skLineSegment(sketch, "E37", {"start": v(0, 5227.84) * mm, "end": v(0, -5440.7) * mm, "construction": true});
            skPoint(sketch, "E38.visualSharp", {"position": v(-6248.4, 4249.42) * mm});
            skArc(sketch, "E38.filletArc", {"start": v(-5791.2, 4249.42) * mm, "mid": v(-6114.49, 4115.5) * mm, "end": v(-6248.4, 3792.22) * mm});
            skPoint(sketch, "E39.visualSharp", {"position": v(6248.4, 4249.42) * mm});
            skArc(sketch, "E39.filletArc", {"start": v(6248.4, 3792.22) * mm, "mid": v(6114.49, 4115.5) * mm, "end": v(5791.2, 4249.42) * mm});
            skPoint(sketch, "E40.visualSharp", {"position": v(6248.4, -4249.42) * mm});
            skArc(sketch, "E40.filletArc", {"start": v(5791.2, -4249.42) * mm, "mid": v(6114.49, -4115.5) * mm, "end": v(6248.4, -3792.22) * mm});
            skPoint(sketch, "E41.visualSharp", {"position": v(-6248.4, -4249.42) * mm});
            skArc(sketch, "E41.filletArc", {"start": v(-6248.4, -3792.22) * mm, "mid": v(-6114.49, -4115.5) * mm, "end": v(-5791.2, -4249.42) * mm});
            skSolve(sketch);
        }
        {
            var Q0;
            Q0=qSketchRegion(id+"F10",true);
            extrude(context, id + "F11", {"entities" : qUnion([Q0]), "operationType" : NewBodyOperationType.ADD, "endBound" : BoundingType.SYMMETRIC, "depth" : 152.4 * mm});
        }
        {
            var Q0;
            Q0=qCreatedBy(makeId("Right.planeOp"),FACE);
            var sketch = newSketch(context, id + "F12", { "sketchPlane" : qUnion([Q0])});
            skLineSegment(sketch, "E42", {"start": v(-9525, 0) * mm, "end": v(-9525, 1778) * mm});
            skLineSegment(sketch, "E43", {"start": v(-9525, 1778) * mm, "end": v(-5207, 11303) * mm});
            skLineSegment(sketch, "E44", {"start": v(-5207, 11303) * mm, "end": v(5207, 11303) * mm});
            skLineSegment(sketch, "E45", {"start": v(5207, 11303) * mm, "end": v(9525, 1778) * mm});
            skLineSegment(sketch, "E46", {"start": v(9525, 1778) * mm, "end": v(9525, 0) * mm});
            skLineSegment(sketch, "E47", {"start": v(9525, 0) * mm, "end": v(-9525, 0) * mm});
            skLineSegment(sketch, "E48", {"start": v(0, -2307.15) * mm, "end": v(0, 14569.66) * mm, "construction": true});
            skSolve(sketch);
        }
        {
            var Q0;
            Q0=qSketchRegion(id+"F12",true);
            extrude(context, id + "F13", {"entities" : qUnion([Q0]), "operationType" : NewBodyOperationType.ADD, "endBound" : BoundingType.SYMMETRIC, "depth" : 304.8 * mm});
        }
        {
            var Q0;
            Q0=qCreatedBy(makeId("Right.planeOp"),FACE);
            cPlane(context, id + "F14", {"entities" : qUnion([Q0]), "cplaneType" : CPlaneType.OFFSET, "offset" : 6350 * mm, "width" : 152.4 * mm, "height" : 152.4 * mm});
        }
        {
            var Q0;
            Q0=qCreatedBy(id+"F14.planeOp",FACE);
            var sketch = newSketch(context, id + "F15", { "sketchPlane" : qUnion([Q0])});
            skLineSegment(sketch, "E49", {"start": v(4572, 0) * mm, "end": v(4572, 11303) * mm});
            skLineSegment(sketch, "E50", {"start": v(4572, 11303) * mm, "end": v(5207, 11303) * mm});
            skLineSegment(sketch, "E51", {"start": v(5207, 11303) * mm, "end": v(9525, 1778) * mm});
            skLineSegment(sketch, "E52", {"start": v(9525, 1778) * mm, "end": v(9525, 0) * mm});
            skLineSegment(sketch, "E53", {"start": v(9525, 0) * mm, "end": v(4572, 0) * mm});
            skLineSegment(sketch, "E54", {"start": v(0, -1220.16) * mm, "end": v(0, 13301) * mm, "construction": true});
            skLineSegment(sketch, "E55.MirrorCS", {"start": v(-4572, 11303) * mm, "end": v(-5207, 11303) * mm});
            skLineSegment(sketch, "E56.MirrorCS", {"start": v(-4572, 0) * mm, "end": v(-4572, 11303) * mm});
            skLineSegment(sketch, "E57.MirrorCS", {"start": v(-5207, 11303) * mm, "end": v(-9525, 1778) * mm});
            skLineSegment(sketch, "E58.MirrorCS", {"start": v(-9525, 1778) * mm, "end": v(-9525, 0) * mm});
            skLineSegment(sketch, "E59.MirrorCS", {"start": v(-9525, 0) * mm, "end": v(-4572, 0) * mm});
            skSolve(sketch);
        }
        {
            var Q0;
            Q0=qSketchRegion(id+"F15",true);
            extrude(context, id + "F16", {"entities" : qUnion([Q0]), "operationType" : NewBodyOperationType.ADD, "endBound" : BoundingType.SYMMETRIC, "depth" : 355.6 * mm});
        }
        {
            var Q0;
            Q0=qCreatedBy(makeId("Right.planeOp"),FACE);
            cPlane(context, id + "F17", {"entities" : qUnion([Q0]), "cplaneType" : CPlaneType.OFFSET, "offset" : 6350 * mm, "oppositeDirection" : true, "width" : 152.4 * mm, "height" : 152.4 * mm});
        }
        {
            var Q0;
            Q0=qCreatedBy(id+"F17.planeOp",FACE);
            var sketch = newSketch(context, id + "F18", { "sketchPlane" : qUnion([Q0])});
            skLineSegment(sketch, "E60", {"start": v(4572, 0) * mm, "end": v(4572, 11303) * mm});
            skLineSegment(sketch, "E61", {"start": v(4572, 11303) * mm, "end": v(5207, 11303) * mm});
            skLineSegment(sketch, "E62", {"start": v(5207, 11303) * mm, "end": v(9525, 1778) * mm});
            skLineSegment(sketch, "E63", {"start": v(9525, 1778) * mm, "end": v(9525, 0) * mm});
            skLineSegment(sketch, "E64", {"start": v(9525, 0) * mm, "end": v(4572, 0) * mm});
            skLineSegment(sketch, "E65", {"start": v(0, -2703.1) * mm, "end": v(0, 13730.2) * mm, "construction": true});
            skLineSegment(sketch, "E66.MirrorCS", {"start": v(-4572, 11303) * mm, "end": v(-5207, 11303) * mm});
            skLineSegment(sketch, "E67.MirrorCS", {"start": v(-5207, 11303) * mm, "end": v(-9525, 1778) * mm});
            skLineSegment(sketch, "E68.MirrorCS", {"start": v(-4572, 0) * mm, "end": v(-4572, 11303) * mm});
            skLineSegment(sketch, "E69.MirrorCS", {"start": v(-9525, 1778) * mm, "end": v(-9525, 0) * mm});
            skLineSegment(sketch, "E70.MirrorCS", {"start": v(-9525, 0) * mm, "end": v(-4572, 0) * mm});
            skSolve(sketch);
        }
        {
            var Q0;
            Q0=qSketchRegion(id+"F18",true);
            extrude(context, id + "F19", {"entities" : qUnion([Q0]), "operationType" : NewBodyOperationType.ADD, "endBound" : BoundingType.SYMMETRIC, "depth" : 355.6 * mm});
        }
        {
            var Q0;
            Q0=qCreatedBy(makeId("Top.planeOp"),FACE);
            var sketch = newSketch(context, id + "F20", { "sketchPlane" : qUnion([Q0])});
            skLineSegment(sketch, "E71", {"start": v(-10922, -5842) * mm, "end": v(-10922, 5842) * mm});
            skLineSegment(sketch, "E72", {"start": v(-10922, 5842) * mm, "end": v(-6858, 9906) * mm});
            skLineSegment(sketch, "E73", {"start": v(-6858, 9906) * mm, "end": v(6858, 9906) * mm});
            skLineSegment(sketch, "E74", {"start": v(6858, 9906) * mm, "end": v(10922, 5842) * mm});
            skLineSegment(sketch, "E75", {"start": v(10922, 5842) * mm, "end": v(10922, -5842) * mm});
            skLineSegment(sketch, "E76", {"start": v(10922, -5842) * mm, "end": v(6858, -9906) * mm});
            skLineSegment(sketch, "E77", {"start": v(6858, -9906) * mm, "end": v(-6858, -9906) * mm});
            skLineSegment(sketch, "E78", {"start": v(-6858, -9906) * mm, "end": v(-10922, -5842) * mm});
            skLineSegment(sketch, "E79", {"start": v(0, 11047.18) * mm, "end": v(0, -11914.8) * mm, "construction": true});
            skLineSegment(sketch, "E80", {"start": v(-11304.08, 0) * mm, "end": v(12211.2, 0) * mm, "construction": true});
            skCircle(sketch, "E81", {"center": v(4318, 7366) * mm, "radius": 558.8 * mm});
            skCircle(sketch, "E82", {"center": v(8382, 2540) * mm, "radius": 558.8 * mm});
            skCircle(sketch, "E83.MirrorC", {"center": v(4318, -7366) * mm, "radius": 558.8 * mm});
            skCircle(sketch, "E84.MirrorC", {"center": v(8382, -2540) * mm, "radius": 558.8 * mm});
            skCircle(sketch, "E85.MirrorC", {"center": v(-4318, -7366) * mm, "radius": 558.8 * mm});
            skCircle(sketch, "E86.MirrorC", {"center": v(-4318, 7366) * mm, "radius": 558.8 * mm});
            skCircle(sketch, "E87.MirrorC", {"center": v(-8382, 2540) * mm, "radius": 558.8 * mm});
            skCircle(sketch, "E88.MirrorC", {"center": v(-8382, -2540) * mm, "radius": 558.8 * mm});
            skSolve(sketch);
        }
        {
            var Q0;
            Q0=qSketchRegion(id+"F20",true);
            extrude(context, id + "F21", {"entities" : qUnion([Q0]), "operationType" : NewBodyOperationType.ADD, "depth" : 1143 * mm});
        }
        {
            var Q0;
            Q0=qCreatedBy(makeId("Top.planeOp"),FACE);
            cPlane(context, id + "F22", {"entities" : qUnion([Q0]), "cplaneType" : CPlaneType.OFFSET, "offset" : 241300 * mm, "width" : 152.4 * mm, "height" : 152.4 * mm});
        }
        {
            var Q0;
            Q0=qCreatedBy(id+"F22.planeOp",FACE);
            var sketch = newSketch(context, id + "F23", { "sketchPlane" : qUnion([Q0])});
            skLineSegment(sketch, "E89", {"start": v(-25400, 2540) * mm, "end": v(-25400, -2540) * mm});
            skLineSegment(sketch, "E90", {"start": v(-25400, -2540) * mm, "end": v(-15240, -2540) * mm});
            skLineSegment(sketch, "E91", {"start": v(-15240, -2540) * mm, "end": v(-9525, -6985) * mm});
            skLineSegment(sketch, "E92", {"start": v(-9525, -6985) * mm, "end": v(9525, -6985) * mm});
            skLineSegment(sketch, "E93", {"start": v(9525, -6985) * mm, "end": v(15240, -2540) * mm});
            skLineSegment(sketch, "E94", {"start": v(15240, -2540) * mm, "end": v(25400, -2540) * mm});
            skLineSegment(sketch, "E95", {"start": v(25400, -2540) * mm, "end": v(25400, 2540) * mm});
            skLineSegment(sketch, "E96", {"start": v(25400, 2540) * mm, "end": v(15240, 2540) * mm});
            skLineSegment(sketch, "E97", {"start": v(15240, 2540) * mm, "end": v(9525, 6985) * mm});
            skLineSegment(sketch, "E98", {"start": v(9525, 6985) * mm, "end": v(-9525, 6985) * mm});
            skLineSegment(sketch, "E99", {"start": v(-9525, 6985) * mm, "end": v(-15240, 2540) * mm});
            skLineSegment(sketch, "E100", {"start": v(-15240, 2540) * mm, "end": v(-25400, 2540) * mm});
            skLineSegment(sketch, "E101", {"start": v(-12700, 0) * mm, "end": v(-8509, 4572) * mm});
            skLineSegment(sketch, "E102", {"start": v(-8509, 4572) * mm, "end": v(8509, 4572) * mm});
            skLineSegment(sketch, "E103", {"start": v(8509, 4572) * mm, "end": v(12700, 0) * mm});
            skLineSegment(sketch, "E104", {"start": v(12700, 0) * mm, "end": v(8509, -4572) * mm});
            skLineSegment(sketch, "E105", {"start": v(8509, -4572) * mm, "end": v(-8509, -4572) * mm});
            skLineSegment(sketch, "E106", {"start": v(-8509, -4572) * mm, "end": v(-12700, 0) * mm});
            skLineSegment(sketch, "E107", {"start": v(0, 9266.93) * mm, "end": v(0, -9722.2) * mm, "construction": true});
            skLineSegment(sketch, "E108", {"start": v(-26607.47, 0) * mm, "end": v(25005.8, 0) * mm, "construction": true});
            skSolve(sketch);
        }
        {
            var Q0;
            Q0=qSketchRegion(id+"F23",true);
            extrude(context, id + "F24", {"entities" : qUnion([Q0]), "operationType" : NewBodyOperationType.ADD, "endBound" : BoundingType.SYMMETRIC, "depth" : 5080 * mm});
        }
    });
